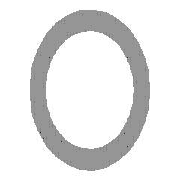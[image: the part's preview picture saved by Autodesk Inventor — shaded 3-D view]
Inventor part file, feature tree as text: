
AUTODESK INVENTOR PART (.ipt)
format: ipt  version: 2021 (Build 250183000, 183)  size: 113,152 bytes
history: native  units: mm (DEFAULTED — no unit token found)
features: other x4, sketch x3, extrude x1, plane x1
ambient origin geometry x8: Origin, YZ Plane, XZ Plane, XY Plane, X Axis, Y Axis, Z Axis, Center Point
bodies: Solid1 (feature_tree)
feature tree (9):
  parser-record x1  (decoder bookkeeping rows leaked as tree rows — omitted from the tree; the rows remain in map.json)
  other  "Driven Length"
  other  "Plano inicial"
  other  "Plano final"
  extrude  "Cuerpo"  Depth=2.8702mm
  sketch  "Boceto"  dims[d4=-0.0mm d5=150.0mm d6=90.0deg d7=150.0mm]
  sketch  "Sketch3"  dims[d0=26.67mm d1=2.8702mm]
  plane  "Work Plane3"
  sketch  "Sketch4"  dims[d2=150.0mm d3=0.0mm]
